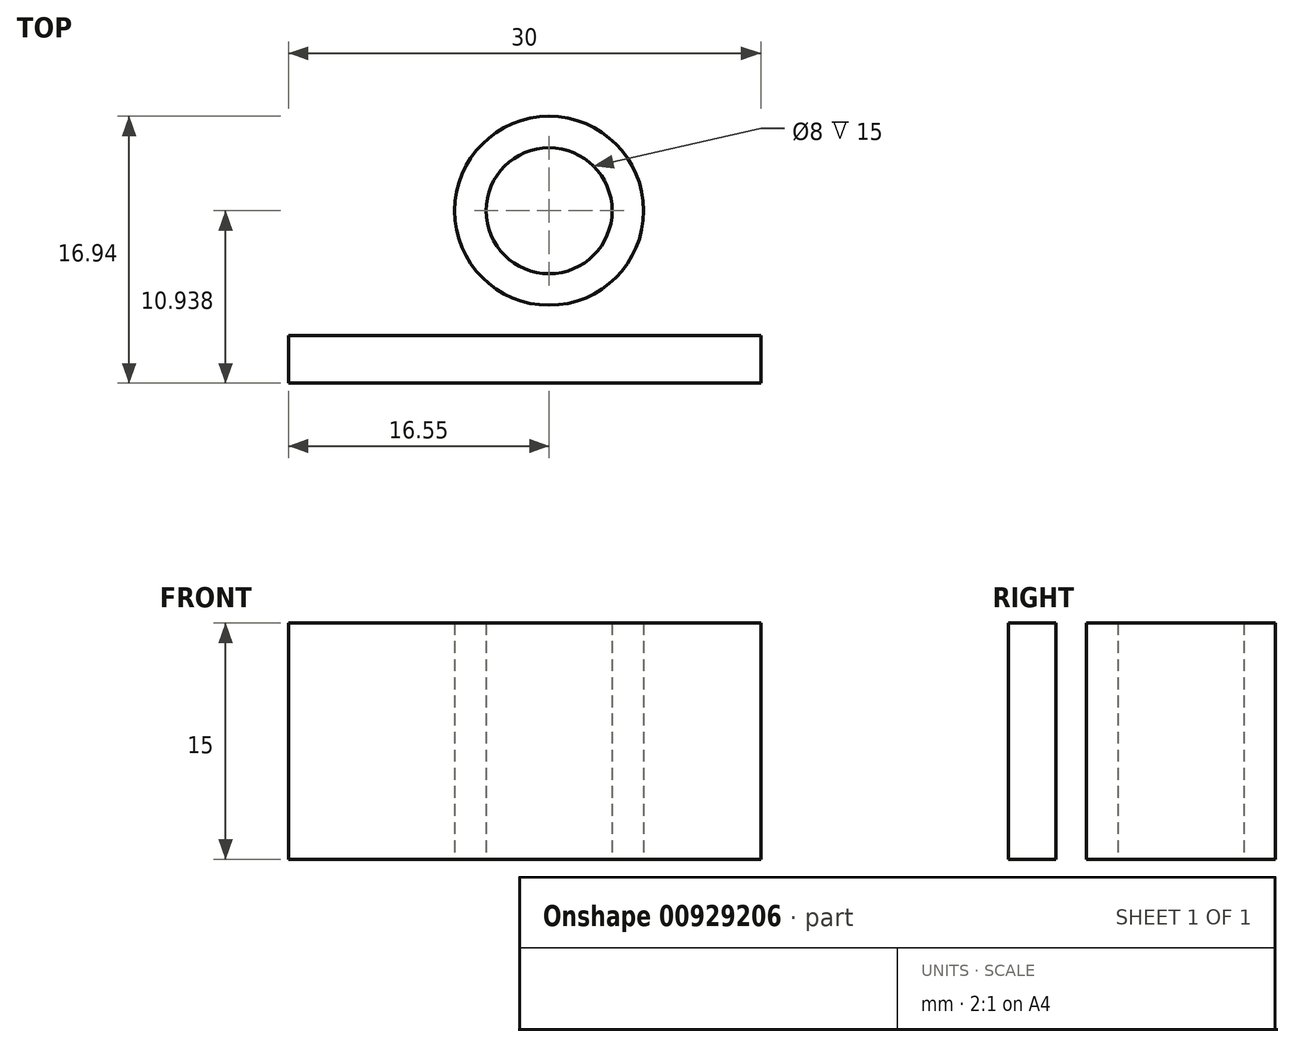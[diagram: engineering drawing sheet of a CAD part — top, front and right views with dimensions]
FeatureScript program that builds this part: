
annotation { "Feature Type Name" : "Feature", "Feature Type Description" : "" }
export const myFeature = defineFeature(function(context is Context, id is Id, definition is map)
    precondition{}
    {
        {
            var Q0;
            Q0=qCreatedBy(makeId("Top.planeOp"),FACE);
            var sketch = newSketch(context, id + "F0", { "sketchPlane" : qUnion([Q0])});
            skLineSegment(sketch, "E0.bottom", {"start": v(-16.55, 0) * mm, "end": v(13.45, 0) * mm});
            skLineSegment(sketch, "E0.top", {"start": v(-16.55, 3) * mm, "end": v(13.45, 3) * mm});
            skLineSegment(sketch, "E0.left", {"start": v(-16.55, 0) * mm, "end": v(-16.55, 3) * mm});
            skLineSegment(sketch, "E0.right", {"start": v(13.45, 0) * mm, "end": v(13.45, 3) * mm});
            skCircle(sketch, "E1", {"center": v(0, 10.94) * mm, "radius": 6 * mm});
            skCircle(sketch, "E2", {"center": v(0, 10.94) * mm, "radius": 4 * mm});
            skSolve(sketch);
        }
        {
            var Q0;
            Q0=makeQuery(id+"F0.imprint","IMPRINT",FACE,{"disambiguationData":[TD([[makeQuery(id+"F0.imprint","IMPRINT",EDGE,{"derivedFrom":sQuery(id+"F0.wireOp",EDGE,"E0.bottom")}),1.0]])]});
            var Q1;
            Q1=makeQuery(id+"F0.imprint","IMPRINT",FACE,{"disambiguationData":[TD([[makeQuery(id+"F0.imprint","IMPRINT",EDGE,{"derivedFrom":sQuery(id+"F0.wireOp",EDGE,"E1")}),1.0]])]});
            extrude(context, id + "F1", {"entities" : qUnion([Q0, Q1]), "depth" : 15 * mm, "offsetDistance" : 25 * mm});
        }
    });
